# Revit family: EP-909-EB_RFA
name_source: partatom
category: Aparatos sanitarios
units: mm (PartAtom-declared; Revit-internal decimal feet)

## family parameters
Activar corte en vistas = No
Compartido = Sí
Corte con vacíos al cargar = No
Cota de conector redondo = Usar diámetro
Mantener orientación de anotación = No
Número OmniClass = 23.45.55.14
Punto de cálculo de habitación = Sí
Se basa en plano de trabajo = Sí
Siempre vertical = Sí
Tipo de pieza = Normal
Título OmniClass = Single Faucets

## types (1)
- EP-909-EB
    Comentarios de tipo = Monomando de lavabo con contra de push Premier Ébano
    Descripción = Llave de lavabo Premier Ébano
    Elevación por defecto = 1"
    Fabricante = HELVEX S.A de C.V.
    Features = Incluye inserto para rebosadero y herramienta para sujeción
    Imagen de tipo = EP-909-EB.jpg
    Inlet Threads = ½" - 14 NPSM
    Max. Working Pressure = 85.3 psi
    Min. Working Pressure = 8.5 psi
    Modelo = EP-909-EB
    Total Height = 5"
    Total Length = 7"
    Total Width = 2"
    URL = https://helvex.com.mx
    Ébano = Ébano

## geometry (parser evidence)
native form markers: Sweep x3
no freeform markers — native parametric forms only
